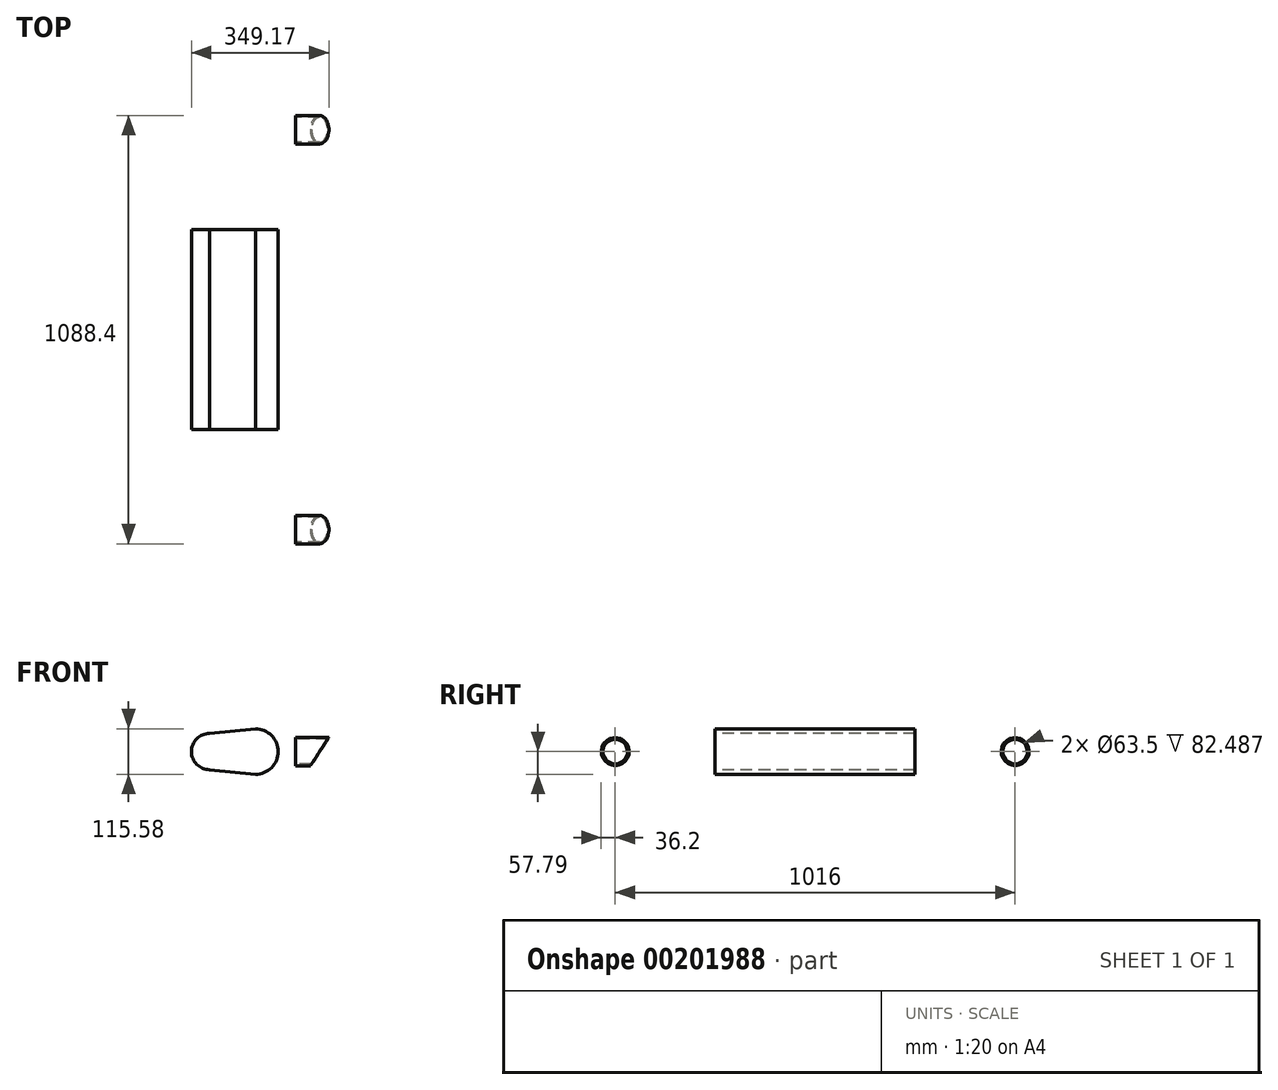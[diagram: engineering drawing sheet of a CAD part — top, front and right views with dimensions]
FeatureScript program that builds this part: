
annotation { "Feature Type Name" : "Feature", "Feature Type Description" : "" }
export const myFeature = defineFeature(function(context is Context, id is Id, definition is map)
    precondition{}
    {
        {
            var Q0;
            Q0=qCreatedBy(makeId("Front.planeOp"),FACE);
            var sketch = newSketch(context, id + "F0", { "sketchPlane" : qUnion([Q0])});
            skArc(sketch, "E0", {"start": v(0, 57.79) * mm, "mid": v(57.79, 0) * mm, "end": v(0, -57.79) * mm});
            skLineSegment(sketch, "E1", {"start": v(0, 0) * mm, "end": v(-72.06, 0) * mm});
            skLineSegment(sketch, "E2", {"start": v(0, 57.79) * mm, "end": v(-116.4, 46.07) * mm});
            skLineSegment(sketch, "E3.MirrorCS", {"start": v(0, -57.79) * mm, "end": v(-116.4, -46.07) * mm});
            skArc(sketch, "E4", {"start": v(-116.4, -46.07) * mm, "mid": v(-162.48, 0) * mm, "end": v(-116.4, 46.07) * mm});
            skSolve(sketch);
        }
        {
            var Q0;
            Q0 = qSketchRegion(id + "F0", true);
            extrude(context, id + "F1", {"entities" : qUnion([Q0]), "oppositeDirection" : true, "depth" : 508 * mm});
        }
        {
            var Q0;
            Q0=qCreatedBy(makeId("Right.planeOp"),FACE);
            var sketch = newSketch(context, id + "F2", { "sketchPlane" : qUnion([Q0])});
            skLineSegment(sketch, "E5", {"start": v(0, 0) * mm, "end": v(-152.4, 0) * mm});
            skLineSegment(sketch, "E6", {"start": v(254, 123.12) * mm, "end": v(254, -122) * mm});
            skLineSegment(sketch, "E7.MirrorCS", {"start": v(508, 0) * mm, "end": v(660.4, 0) * mm});
            skSolve(sketch);
        }
        {
            var Q0;
            Q0=qCreatedBy(makeId("Top.planeOp"),FACE);
            var sketch = newSketch(context, id + "F3", { "sketchPlane" : qUnion([Q0])});
            skArc(sketch, "E8", {"start": v(0, -152.4) * mm, "mid": v(29.76, -224.24) * mm, "end": v(101.6, -254) * mm});
            skLineSegment(sketch, "E9", {"start": v(-251.46, 254) * mm, "end": v(207.7, 254) * mm});
            skArc(sketch, "E10.MirrorCS", {"start": v(0, 660.4) * mm, "mid": v(29.76, 732.24) * mm, "end": v(101.6, 762) * mm});
            skSolve(sketch);
        }
        {
            var Q0;
            Q0=makeQuery(id+"F1.opExtrude","CAP_FACE",FACE,{"disambiguationData":[OSD([sQuery(id+"F0.wireOp",EDGE,"E0"),sQuery(id+"F0.wireOp",EDGE,"E2"),sQuery(id+"F0.wireOp",EDGE,"E3.MirrorCS"),sQuery(id+"F0.wireOp",EDGE,"E4")])],"isStart":true});
            var sketch = newSketch(context, id + "F4", { "sketchPlane" : qUnion([Q0])});
            skCircle(sketch, "E11", {"center": v(0, 0) * mm, "radius": 31.75 * mm});
            skCircle(sketch, "E12", {"center": v(0, 0) * mm, "radius": 25.4 * mm});
            skSolve(sketch);
        }
        {
            var Q0;
            Q0=makeQuery(id+"F1.opExtrude","CAP_FACE",FACE,{"disambiguationData":[OSD([sQuery(id+"F0.wireOp",EDGE,"E0"),sQuery(id+"F0.wireOp",EDGE,"E2"),sQuery(id+"F0.wireOp",EDGE,"E3.MirrorCS"),sQuery(id+"F0.wireOp",EDGE,"E4")])],"isStart":false});
            var sketch = newSketch(context, id + "F5", { "sketchPlane" : qUnion([Q0])});
            skCircle(sketch, "E13", {"center": v(0, 0) * mm, "radius": 25.4 * mm});
            skCircle(sketch, "E14", {"center": v(0, 0) * mm, "radius": 31.75 * mm});
            skSolve(sketch);
        }
        {
            var Q0;
            Q0=makeQuery(id+"F4.imprint","IMPRINT",FACE,{"disambiguationData":[TD([[makeQuery(id+"F4.imprint","IMPRINT",EDGE,{"derivedFrom":sQuery(id+"F4.wireOp",EDGE,"E12")}),1.0]])]});
            var Q1;
            Q1=sQuery(id+"F4.wireOp",EDGE,"E11");
            var Q2;
            Q2=sQuery(id+"F4.wireOp",EDGE,"E12");
            var Q3;
            Q3=sQuery(id+"F2.wireOp",EDGE,"E5");
            var Q4;
            Q4=sQuery(id+"F3.wireOp",EDGE,"E8");
            sweep(context, id + "F6", {"bodyType" : ToolBodyType.SURFACE, "profiles" : qUnion([Q0]), "surfaceProfiles" : qUnion([Q1, Q2]), "path" : qUnion([Q3, Q4])});
        }
        {
            var Q0;
            Q0=makeQuery(id+"F1.opExtrude","CAP_FACE",FACE,{"disambiguationData":[OSD([sQuery(id+"F0.wireOp",EDGE,"E0"),sQuery(id+"F0.wireOp",EDGE,"E2"),sQuery(id+"F0.wireOp",EDGE,"E3.MirrorCS"),sQuery(id+"F0.wireOp",EDGE,"E4")])],"isStart":true});
            var Q1;
            Q1=makeQuery(id+"F5.imprint","IMPRINT",FACE,{"disambiguationData":[TD([[makeQuery(id+"F5.imprint","IMPRINT",EDGE,{"derivedFrom":sQuery(id+"F5.wireOp",EDGE,"E14")}),-1.0]])]});
            cPlane(context, id + "F7", {"entities" : qUnion([Q0, Q1]), "cplaneType" : CPlaneType.MID_PLANE, "offset" : 25.4 * mm, "width" : 152.4 * mm, "height" : 152.4 * mm});
        }
        {
            var Q0;
            Q0=makeQuery(id+"F1.opExtrude","CAP_FACE",FACE,{"disambiguationData":[OSD([sQuery(id+"F0.wireOp",EDGE,"E0"),sQuery(id+"F0.wireOp",EDGE,"E2"),sQuery(id+"F0.wireOp",EDGE,"E3.MirrorCS"),sQuery(id+"F0.wireOp",EDGE,"E4")])],"isStart":true});
            var sketch = newSketch(context, id + "F8", { "sketchPlane" : qUnion([Q0])});
            skCircle(sketch, "E15", {"center": v(0, 0) * mm, "radius": 19.78 * mm});
            skCircle(sketch, "E16", {"center": v(0, 0) * mm, "radius": 30.11 * mm});
            skSolve(sketch);
        }
        {
            var Q0;
            Q0=makeQuery(id+"F5.imprint","IMPRINT",FACE,{"disambiguationData":[TD([[makeQuery(id+"F5.imprint","IMPRINT",EDGE,{"derivedFrom":sQuery(id+"F5.wireOp",EDGE,"E13")}),-1.0]])]});
            var Q1;
            Q1=sQuery(id+"F5.wireOp",EDGE,"E13");
            var Q2;
            Q2=sQuery(id+"F5.wireOp",EDGE,"E14");
            var Q3;
            Q3=sQuery(id+"F2.wireOp",EDGE,"E7.MirrorCS");
            var Q4;
            Q4=sQuery(id+"F3.wireOp",EDGE,"E10.MirrorCS");
            sweep(context, id + "F9", {"bodyType" : ToolBodyType.SURFACE, "profiles" : qUnion([Q0]), "surfaceProfiles" : qUnion([Q1, Q2]), "path" : qUnion([Q3, Q4])});
        }
        {
            var Q0;
            Q0=qCreatedBy(makeId("Right.planeOp"),FACE);
            cPlane(context, id + "F10", {"entities" : qUnion([Q0]), "cplaneType" : CPlaneType.OFFSET, "offset" : 101.6 * mm, "width" : 152.4 * mm, "height" : 152.4 * mm});
        }
        {
            var Q0;
            Q0=qCreatedBy(id+"F10.planeOp",FACE);
            var sketch = newSketch(context, id + "F11", { "sketchPlane" : qUnion([Q0])});
            skCircle(sketch, "E17", {"center": v(762, 0) * mm, "radius": 31.75 * mm});
            skCircle(sketch, "E18", {"center": v(762, 0) * mm, "radius": 36.2 * mm});
            skSolve(sketch);
        }
        {
            var Q0;
            Q0 = qSketchRegion(id + "F11", true);
            extrude(context, id + "F12", {"entities" : qUnion([Q0]), "depth" : 101.6 * mm});
        }
        {
            var Q0;
            Q0=makeQuery(id+"F12.opExtrude","SWEPT_BODY",BODY,{"disambiguationData":[OSD([sQuery(id+"F11.wireOp",EDGE,"E17"),sQuery(id+"F11.wireOp",EDGE,"E18")])]});
            var Q1;
            Q1=qCreatedBy(id+"F7.planeOp",FACE);
            mirror(context, id + "F13", {"entities" : qUnion([Q0]), "mirrorPlane" : qUnion([Q1])});
        }
        {
            var Q0;
            Q0=qCreatedBy(makeId("Front.planeOp"),FACE);
            cPlane(context, id + "F14", {"entities" : qUnion([Q0]), "cplaneType" : CPlaneType.OFFSET, "offset" : 290.2 * mm, "width" : 152.4 * mm, "height" : 152.4 * mm});
        }
        {
            var Q0;
            Q0=qCreatedBy(id+"F14.planeOp",FACE);
            var sketch = newSketch(context, id + "F15", { "sketchPlane" : qUnion([Q0])});
            skLineSegment(sketch, "E19", {"start": v(203.2, 36.2) * mm, "end": v(186.7, 36.2) * mm});
            skLineSegment(sketch, "E20", {"start": v(186.7, 36.2) * mm, "end": v(139.7, -36.2) * mm});
            skLineSegment(sketch, "E21", {"start": v(203.2, -36.2) * mm, "end": v(139.7, -36.2) * mm});
            skLineSegment(sketch, "E22", {"start": v(203.2, 36.2) * mm, "end": v(203.2, -36.2) * mm});
            skSolve(sketch);
        }
        {
            var Q0;
            Q0 = qSketchRegion(id + "F15", true);
            extrude(context, id + "F16", {"entities" : qUnion([Q0]), "operationType" : NewBodyOperationType.REMOVE, "oppositeDirection" : true, "depth" : 1270 * mm});
        }
        {
            var Q0;
            Q0=qCreatedBy(id+"F14.planeOp",FACE);
            cPlane(context, id + "F17", {"entities" : qUnion([Q0]), "cplaneType" : CPlaneType.OFFSET, "offset" : 1016 * mm, "oppositeDirection" : true, "width" : 152.4 * mm, "height" : 152.4 * mm});
        }
        {
            var Q0;
            Q0=qCreatedBy(id+"F17.planeOp",FACE);
            var sketch = newSketch(context, id + "F18", { "sketchPlane" : qUnion([Q0])});
            skLineSegment(sketch, "E23", {"start": v(203.2, 36.2) * mm, "end": v(186.7, 36.2) * mm});
            skLineSegment(sketch, "E24", {"start": v(203.2, -36.2) * mm, "end": v(139.7, -36.2) * mm});
            skLineSegment(sketch, "E25", {"start": v(203.2, 36.2) * mm, "end": v(203.2, -36.2) * mm});
            skLineSegment(sketch, "E26", {"start": v(186.7, 36.2) * mm, "end": v(139.7, -36.2) * mm});
            skSolve(sketch);
        }
        {
            var Q0;
            Q0 = qSketchRegion(id + "F18", true);
            extrude(context, id + "F19", {"entities" : qUnion([Q0]), "operationType" : NewBodyOperationType.REMOVE, "oppositeDirection" : true, "depth" : 76.2 * mm});
        }
        {
            var Q0;
            Q0=qCreatedBy(makeId("Right.planeOp"),FACE);
            cPlane(context, id + "F20", {"entities" : qUnion([Q0]), "cplaneType" : CPlaneType.OFFSET, "offset" : 116.4 * mm, "oppositeDirection" : true, "width" : 152.4 * mm, "height" : 152.4 * mm});
        }
        {
            var Q0;
            Q0=qCreatedBy(makeId("Top.planeOp"),FACE);
            var sketch = newSketch(context, id + "F21", { "sketchPlane" : qUnion([Q0])});
            skFitSpline(sketch, "E27", {"points": [v(-116.4, -58.8) * mm, v(-415.15, -232.15) * mm, v(-866.02, -275.53) * mm], "startDerivative": vector(-593.83, -439.62) * mm, "endDerivative": vector(-898.98, -3.75) * mm});
            skFitSpline(sketch, "E28", {"points": [v(-155.84, -87.86) * mm, v(-116.4, -29.49) * mm], "startDerivative": vector(118.29, 87.17) * mm, "endDerivative": vector(0, 50.13) * mm});
            skSolve(sketch);
        }
        {
            var Q0;
            Q0=qCreatedBy(id+"F20.planeOp",FACE);
            var sketch = newSketch(context, id + "F22", { "sketchPlane" : qUnion([Q0])});
            skLineSegment(sketch, "E29", {"start": v(0, 0) * mm, "end": v(-29.49, 0) * mm});
            skSolve(sketch);
        }
        {
            var Q0;
            Q0=makeQuery(id+"F8.imprint","IMPRINT",FACE,{"disambiguationData":[TD([[makeQuery(id+"F8.imprint","IMPRINT",EDGE,{"derivedFrom":sQuery(id+"F8.wireOp",EDGE,"E16")}),-1.0]])]});
            var sketch = newSketch(context, id + "F23", { "sketchPlane" : qUnion([Q0])});
            skCircle(sketch, "E30", {"center": v(-116.4, 0) * mm, "radius": 28.58 * mm});
            skCircle(sketch, "E31", {"center": v(-116.4, 0) * mm, "radius": 34.93 * mm});
            skSolve(sketch);
        }
    });
